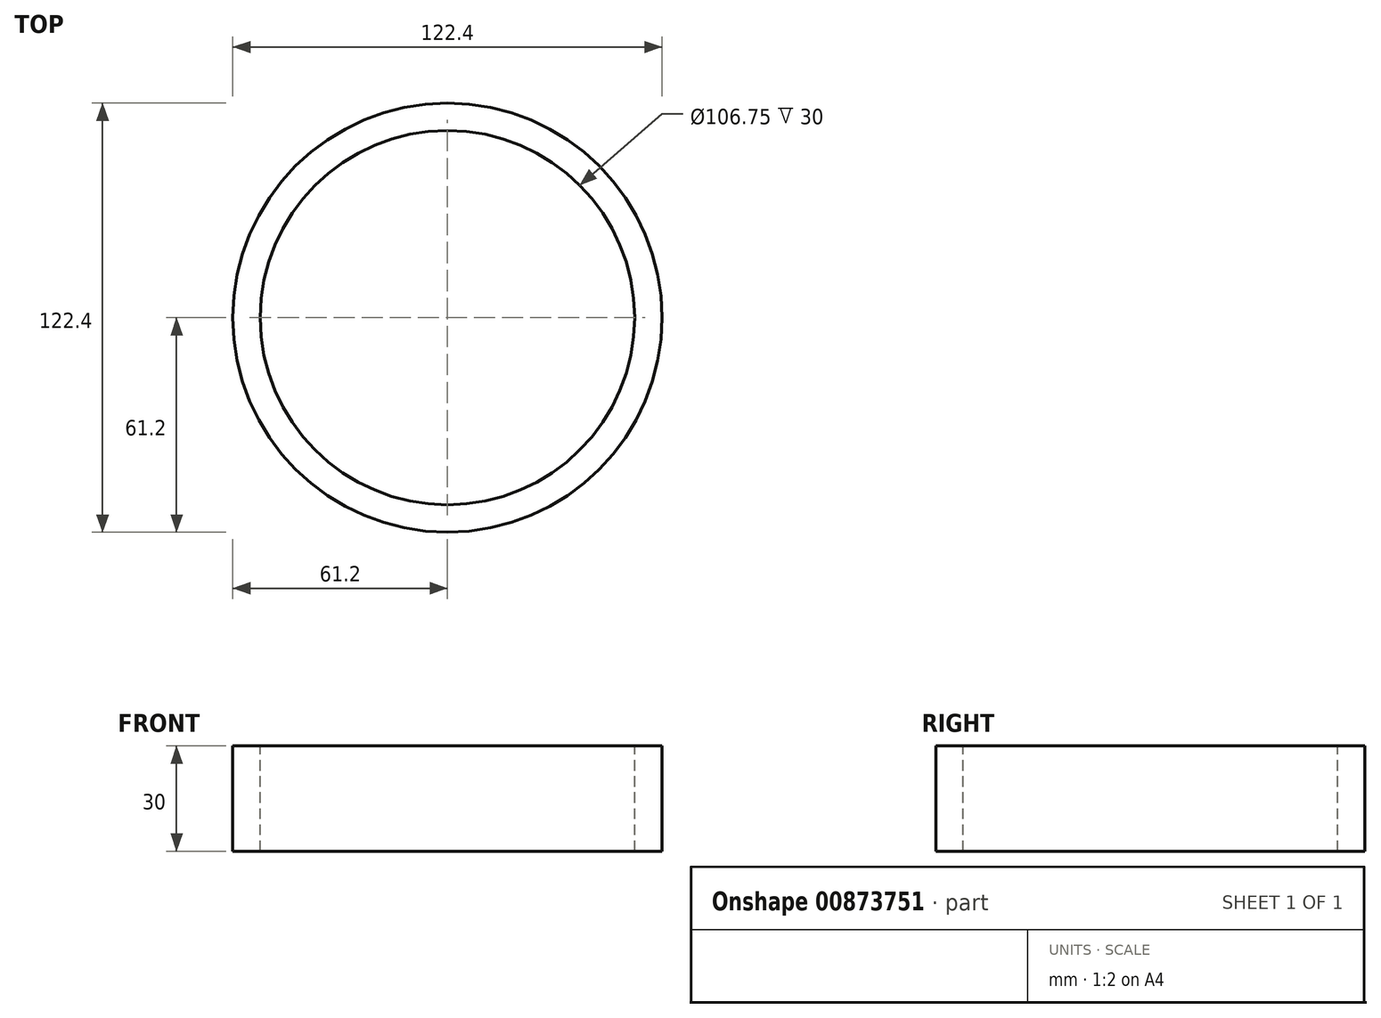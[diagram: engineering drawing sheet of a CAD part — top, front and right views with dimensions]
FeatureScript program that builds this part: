
annotation { "Feature Type Name" : "Feature", "Feature Type Description" : "" }
export const myFeature = defineFeature(function(context is Context, id is Id, definition is map)
    precondition{}
    {
        {
            var Q0;
            Q0=qCreatedBy(makeId("Top.planeOp"),FACE);
            var sketch = newSketch(context, id + "F0", { "sketchPlane" : qUnion([Q0])});
            skCircle(sketch, "E0", {"center": v(0, 0) * mm, "radius": 61.2 * mm});
            skSolve(sketch);
        }
        {
            var Q0;
            Q0=makeQuery(id+"F0.imprint","IMPRINT",FACE,{"disambiguationData":[TD([[makeQuery(id+"F0.imprint","IMPRINT",EDGE,{"derivedFrom":sQuery(id+"F0.wireOp",EDGE,"E0")}),1.0]])]});
            var Q1;
            Q1=sQuery(id+"F0.wireOp",EDGE,"E0");
            extrude(context, id + "F1", {"entities" : qUnion([Q0]), "surfaceEntities" : qUnion([Q1]), "depth" : 30 * mm, "offsetDistance" : 25.4 * mm});
        }
        {
            var Q0;
            Q0=makeQuery(id+"F1.opExtrude","CAP_FACE",FACE,{"disambiguationData":[OSD([sQuery(id+"F0.wireOp",EDGE,"E0")])],"isStart":false});
            var sketch = newSketch(context, id + "F2", { "sketchPlane" : qUnion([Q0])});
            skCircle(sketch, "E1", {"center": v(0, 0) * mm, "radius": 53.38 * mm});
            skSolve(sketch);
        }
        {
            var Q0;
            Q0=makeQuery(id+"F2.imprint","IMPRINT",FACE,{"disambiguationData":[TD([[makeQuery(id+"F2.imprint","IMPRINT",EDGE,{"derivedFrom":sQuery(id+"F2.wireOp",EDGE,"E1")}),1.0]])]});
            var Q1;
            Q1 = qSketchRegion(id + "F2", true);
            extrude(context, id + "F3", {"entities" : qUnion([Q0, Q1]), "operationType" : NewBodyOperationType.REMOVE, "oppositeDirection" : true, "depth" : 45.53 * mm, "offsetDistance" : 25.4 * mm});
        }
    });
